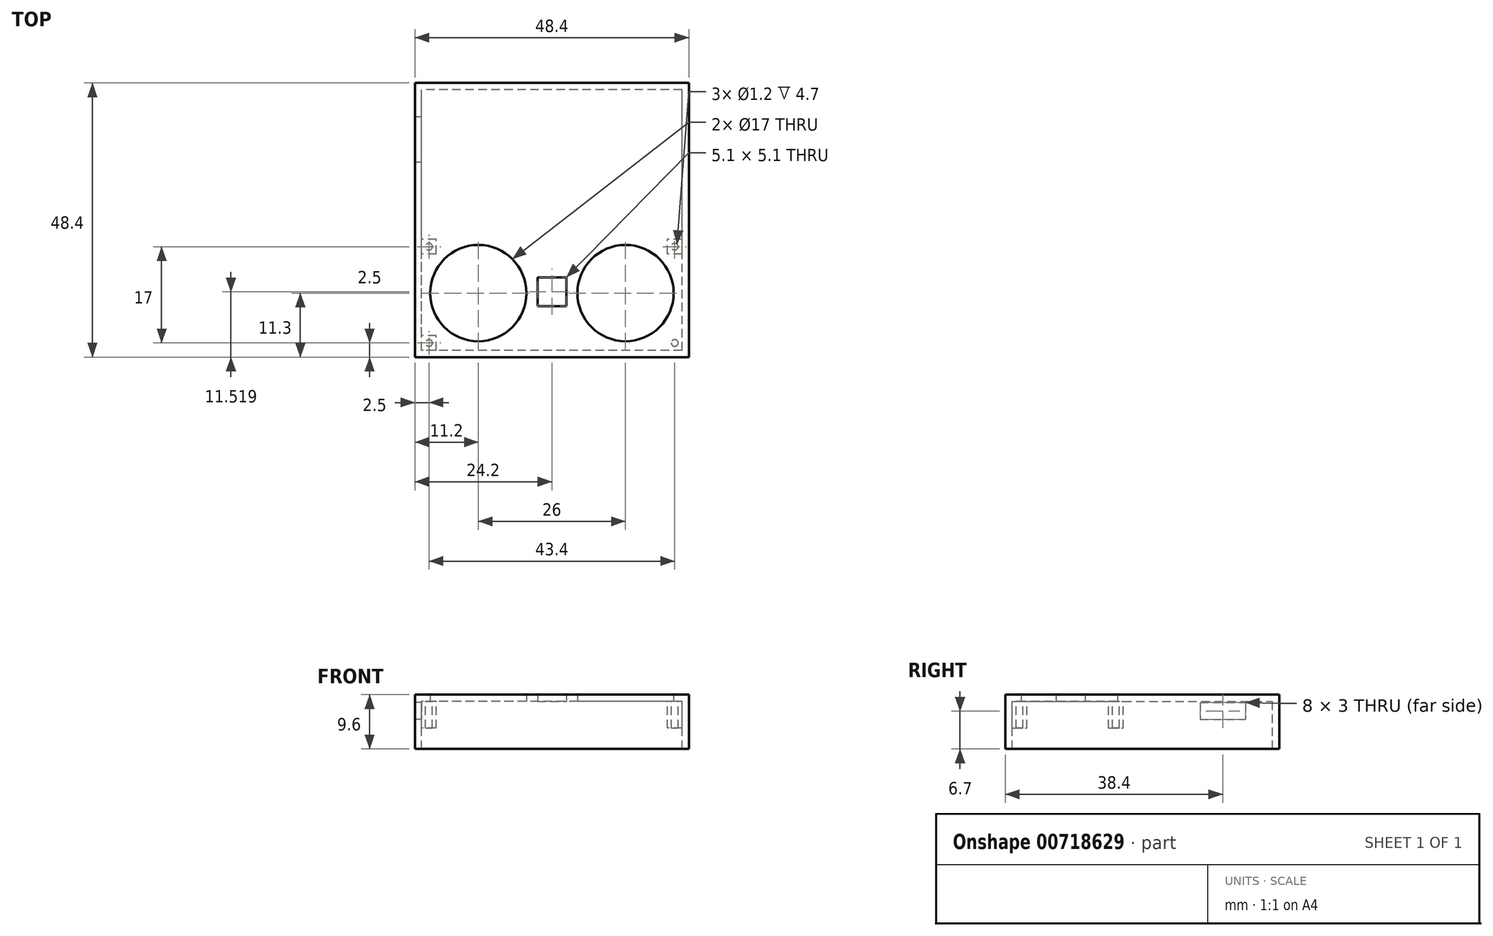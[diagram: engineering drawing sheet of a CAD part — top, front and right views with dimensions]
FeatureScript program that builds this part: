
annotation { "Feature Type Name" : "Feature", "Feature Type Description" : "" }
export const myFeature = defineFeature(function(context is Context, id is Id, definition is map)
    precondition{}
    {
        {
            var Q0;
            Q0=qCreatedBy(makeId("Top.planeOp"),FACE);
            var sketch = newSketch(context, id + "F0", { "sketchPlane" : qUnion([Q0])});
            skLineSegment(sketch, "E0.bottom", {"start": v(0, 0) * mm, "end": v(-23, 0) * mm});
            skLineSegment(sketch, "E0.top", {"start": v(0, 23) * mm, "end": v(-23, 23) * mm});
            skLineSegment(sketch, "E0.left", {"start": v(0, 0) * mm, "end": v(0, 23) * mm});
            skLineSegment(sketch, "E0.right", {"start": v(-23, 0) * mm, "end": v(-23, 23) * mm});
            skLineSegment(sketch, "E1.MirrorCS", {"start": v(-23, 0) * mm, "end": v(-23, -23) * mm});
            skLineSegment(sketch, "E2.MirrorCS", {"start": v(0, 0) * mm, "end": v(0, -23) * mm});
            skLineSegment(sketch, "E3.MirrorCS", {"start": v(0, -23) * mm, "end": v(-23, -23) * mm});
            skLineSegment(sketch, "E4.MirrorCS", {"start": v(0, 23) * mm, "end": v(23, 23) * mm});
            skLineSegment(sketch, "E5.MirrorCS", {"start": v(0, -23) * mm, "end": v(23, -23) * mm});
            skLineSegment(sketch, "E6.MirrorCS", {"start": v(23, 0) * mm, "end": v(23, 23) * mm});
            skLineSegment(sketch, "E7.MirrorCS", {"start": v(0, 0) * mm, "end": v(23, 0) * mm});
            skLineSegment(sketch, "E8.MirrorCS", {"start": v(23, 0) * mm, "end": v(23, -23) * mm});
            skCircle(sketch, "E9", {"center": v(13, -12.9) * mm, "radius": 8.5 * mm});
            skCircle(sketch, "E10", {"center": v(-13, -12.9) * mm, "radius": 8.5 * mm});
            skLineSegment(sketch, "E11.bottom", {"start": v(-2.55, -15.23) * mm, "end": v(2.55, -15.23) * mm});
            skLineSegment(sketch, "E11.top", {"start": v(-2.55, -10.13) * mm, "end": v(2.55, -10.13) * mm});
            skLineSegment(sketch, "E11.left", {"start": v(-2.55, -15.23) * mm, "end": v(-2.55, -10.13) * mm});
            skLineSegment(sketch, "E11.right", {"start": v(2.55, -15.23) * mm, "end": v(2.55, -10.13) * mm});
            skSolve(sketch);
        }
        {
            var Q0;
            {var subQ1=sQuery(id+"F0.wireOp",EDGE,"E0.top");Q0=makeQuery(id+"F0.imprint","IMPRINT",FACE,{"disambiguationData":[TD([[makeQuery(id+"F0.imprint","IMPRINT",EDGE,{"derivedFrom":subQ1}),1.0]])]});}
            var Q1;
            {var subQ1=sQuery(id+"F0.wireOp",EDGE,"E1.MirrorCS");Q1=makeQuery(id+"F0.imprint","IMPRINT",FACE,{"disambiguationData":[TD([[makeQuery(id+"F0.imprint","IMPRINT",EDGE,{"derivedFrom":subQ1}),1.0]])]});}
            var Q2;
            {var subQ7=sQuery(id+"F0.wireOp",EDGE,"E4.MirrorCS");Q2=makeQuery(id+"F0.imprint","IMPRINT",FACE,{"disambiguationData":[TD([[makeQuery(id+"F0.imprint","IMPRINT",EDGE,{"derivedFrom":subQ7}),-1.0]])]});}
            var Q3;
            {var subQ9=sQuery(id+"F0.wireOp",EDGE,"E5.MirrorCS");Q3=makeQuery(id+"F0.imprint","IMPRINT",FACE,{"disambiguationData":[TD([[makeQuery(id+"F0.imprint","IMPRINT",EDGE,{"derivedFrom":subQ9}),1.0]])]});}
            extrude(context, id + "F1", {"entities" : qUnion([Q0, Q1, Q2, Q3]), "endBound" : BoundingType.SYMMETRIC, "depth" : 1.2 * mm, "offsetDistance" : 25 * mm});
        }
        {
            var Q0;
            Q0=makeQuery(id+"F1.opExtrude","CAP_FACE",FACE,{"disambiguationData":[OSD([sQuery(id+"F0.wireOp",EDGE,"E0.top"),sQuery(id+"F0.wireOp",EDGE,"E0.right"),sQuery(id+"F0.wireOp",EDGE,"E1.MirrorCS"),sQuery(id+"F0.wireOp",EDGE,"E3.MirrorCS"),sQuery(id+"F0.wireOp",EDGE,"18OHl2Td-8SmV-nLja-3BuC-y3GKfxBrHoTz"),sQuery(id+"F0.wireOp",EDGE,"E4.MirrorCS"),sQuery(id+"F0.wireOp",EDGE,"f96b6ea1-77e4-4928-808a-502d4fa3524e1.MirrorC"),sQuery(id+"F0.wireOp",EDGE,"E5.MirrorCS"),sQuery(id+"F0.wireOp",EDGE,"E6.MirrorCS"),sQuery(id+"F0.wireOp",EDGE,"E8.MirrorCS"),sQuery(id+"F0.wireOp",EDGE,"ZzQ9hNgQ-oA48-EWd8-CxiW-ZcLfL0NBcqYF")])],"isStart":false});
            var sketch = newSketch(context, id + "F2", { "sketchPlane" : qUnion([Q0])});
            skLineSegment(sketch, "E12.0", {"start": v(23, 23) * mm, "end": v(-23, 23) * mm});
            skLineSegment(sketch, "E12.1", {"start": v(-23, -23) * mm, "end": v(-23, 23) * mm});
            skLineSegment(sketch, "E12.2", {"start": v(23, -23) * mm, "end": v(-23, -23) * mm});
            skLineSegment(sketch, "E12.3", {"start": v(23, -23) * mm, "end": v(23, 23) * mm});
            skPoint(sketch, "E12.4", {"position": v(0, 0) * mm});
            skLineSegment(sketch, "E13.bottom", {"start": v(0, 24.2) * mm, "end": v(-24.2, 24.2) * mm});
            skLineSegment(sketch, "E13.top", {"start": v(0, -24.2) * mm, "end": v(-24.2, -24.2) * mm});
            skLineSegment(sketch, "E13.left", {"start": v(0, 24.2) * mm, "end": v(0, -24.2) * mm});
            skLineSegment(sketch, "E13.right", {"start": v(-24.2, 24.2) * mm, "end": v(-24.2, -24.2) * mm});
            skLineSegment(sketch, "E14.MirrorCS", {"start": v(0, 24.2) * mm, "end": v(24.2, 24.2) * mm});
            skLineSegment(sketch, "E15.MirrorCS", {"start": v(24.2, 24.2) * mm, "end": v(24.2, -24.2) * mm});
            skLineSegment(sketch, "E16.MirrorCS", {"start": v(0, -24.2) * mm, "end": v(24.2, -24.2) * mm});
            skSolve(sketch);
        }
        {
            var Q0;
            {var subQ1=sQuery(id+"F2.wireOp",EDGE,"E12.1");Q0=makeQuery(id+"F2.imprint","IMPRINT",FACE,{"disambiguationData":[TD([[makeQuery(id+"F2.imprint","IMPRINT",EDGE,{"derivedFrom":subQ1}),1.0]])]});}
            var Q1;
            {var subQ4=sQuery(id+"F2.wireOp",EDGE,"E12.3");Q1=makeQuery(id+"F2.imprint","IMPRINT",FACE,{"disambiguationData":[TD([[makeQuery(id+"F2.imprint","IMPRINT",EDGE,{"derivedFrom":subQ4}),-1.0]])]});}
            extrude(context, id + "F3", {"entities" : qUnion([Q0, Q1]), "operationType" : NewBodyOperationType.ADD, "oppositeDirection" : true, "depth" : 9.6 * mm, "offsetDistance" : 25 * mm});
        }
        {
            var Q0;
            Q0=makeQuery(id+"F1.opExtrude","CAP_FACE",FACE,{"disambiguationData":[OSD([sQuery(id+"F0.wireOp",EDGE,"E0.top"),sQuery(id+"F0.wireOp",EDGE,"E0.right"),sQuery(id+"F0.wireOp",EDGE,"E1.MirrorCS"),sQuery(id+"F0.wireOp",EDGE,"E3.MirrorCS"),sQuery(id+"F0.wireOp",EDGE,"18OHl2Td-8SmV-nLja-3BuC-y3GKfxBrHoTz"),sQuery(id+"F0.wireOp",EDGE,"E4.MirrorCS"),sQuery(id+"F0.wireOp",EDGE,"f96b6ea1-77e4-4928-808a-502d4fa3524e1.MirrorC"),sQuery(id+"F0.wireOp",EDGE,"E5.MirrorCS"),sQuery(id+"F0.wireOp",EDGE,"E6.MirrorCS"),sQuery(id+"F0.wireOp",EDGE,"E8.MirrorCS"),sQuery(id+"F0.wireOp",EDGE,"ZzQ9hNgQ-oA48-EWd8-CxiW-ZcLfL0NBcqYF")])],"isStart":true});
            var sketch = newSketch(context, id + "F4", { "sketchPlane" : qUnion([Q0])});
            skLineSegment(sketch, "E17.0", {"start": v(23, 23) * mm, "end": v(-23, 23) * mm});
            skLineSegment(sketch, "E17.1", {"start": v(-23, 23) * mm, "end": v(-23, -23) * mm});
            skLineSegment(sketch, "E17.2", {"start": v(23, -23) * mm, "end": v(-23, -23) * mm});
            skLineSegment(sketch, "E17.3", {"start": v(23, 23) * mm, "end": v(23, -23) * mm});
            skLineSegment(sketch, "E18", {"start": v(-21.7, 23) * mm, "end": v(-21.7, 21.7) * mm, "construction": true});
            skLineSegment(sketch, "E19", {"start": v(-21.7, 21.7) * mm, "end": v(-23, 21.7) * mm, "construction": true});
            skCircle(sketch, "E20", {"center": v(-21.7, 21.7) * mm, "radius": 0.6 * mm});
            skCircle(sketch, "E21.MirrorC", {"center": v(21.7, 21.7) * mm, "radius": 0.6 * mm});
            skLineSegment(sketch, "E22.bottom", {"start": v(-20.4, 23) * mm, "end": v(-23, 23) * mm});
            skLineSegment(sketch, "E22.top", {"start": v(-20.4, 20.4) * mm, "end": v(-23, 20.4) * mm});
            skLineSegment(sketch, "E22.left", {"start": v(-20.4, 23) * mm, "end": v(-20.4, 20.4) * mm});
            skLineSegment(sketch, "E22.right", {"start": v(-23, 23) * mm, "end": v(-23, 20.4) * mm});
            skLineSegment(sketch, "E23.MirrorCS", {"start": v(20.4, 23) * mm, "end": v(20.4, 20.4) * mm});
            skLineSegment(sketch, "E24.MirrorCS", {"start": v(20.4, 20.4) * mm, "end": v(23, 20.4) * mm});
            skLineSegment(sketch, "E25", {"start": v(-21.7, 6) * mm, "end": v(-21.7, 4.7) * mm, "construction": true});
            skLineSegment(sketch, "E26", {"start": v(-21.7, 4.7) * mm, "end": v(-23, 4.7) * mm, "construction": true});
            skCircle(sketch, "E27", {"center": v(-21.7, 4.7) * mm, "radius": 0.6 * mm});
            skLineSegment(sketch, "E28.bottom", {"start": v(-20.4, 6) * mm, "end": v(-23, 6) * mm});
            skLineSegment(sketch, "E28.top", {"start": v(-20.4, 3.4) * mm, "end": v(-23, 3.4) * mm});
            skLineSegment(sketch, "E28.left", {"start": v(-20.4, 6) * mm, "end": v(-20.4, 3.4) * mm});
            skLineSegment(sketch, "E28.right", {"start": v(-23, 6) * mm, "end": v(-23, 3.4) * mm});
            skLineSegment(sketch, "E29", {"start": v(21.7, 6) * mm, "end": v(21.7, 4.7) * mm, "construction": true});
            skLineSegment(sketch, "E30", {"start": v(21.7, 4.7) * mm, "end": v(20.4, 4.7) * mm, "construction": true});
            skCircle(sketch, "E31", {"center": v(21.7, 4.7) * mm, "radius": 0.6 * mm});
            skLineSegment(sketch, "E32.bottom", {"start": v(23, 6) * mm, "end": v(20.4, 6) * mm});
            skLineSegment(sketch, "E32.top", {"start": v(23, 3.4) * mm, "end": v(20.4, 3.4) * mm});
            skLineSegment(sketch, "E32.left", {"start": v(23, 6) * mm, "end": v(23, 3.4) * mm});
            skLineSegment(sketch, "E32.right", {"start": v(20.4, 6) * mm, "end": v(20.4, 3.4) * mm});
            skSolve(sketch);
        }
        {
            var Q0;
            Q0=makeQuery(id+"F4.imprint","IMPRINT",FACE,{"disambiguationData":[TD([[makeQuery(id+"F4.imprint","IMPRINT",EDGE,{"derivedFrom":sQuery(id+"F4.wireOp",EDGE,"E21.MirrorC")}),1.0]])]});
            var Q1;
            Q1=makeQuery(id+"F4.imprint","IMPRINT",FACE,{"disambiguationData":[TD([[makeQuery(id+"F4.imprint","IMPRINT",EDGE,{"derivedFrom":sQuery(id+"F4.wireOp",EDGE,"E20")}),-1.0]])]});
            var Q2;
            Q2=makeQuery(id+"F4.imprint","IMPRINT",FACE,{"disambiguationData":[TD([[makeQuery(id+"F4.imprint","IMPRINT",EDGE,{"derivedFrom":sQuery(id+"F4.wireOp",EDGE,"E27")}),-1.0]])]});
            var Q3;
            Q3=makeQuery(id+"F4.imprint","IMPRINT",FACE,{"disambiguationData":[TD([[makeQuery(id+"F4.imprint","IMPRINT",EDGE,{"derivedFrom":sQuery(id+"F4.wireOp",EDGE,"E31")}),-1.0]])]});
            extrude(context, id + "F5", {"entities" : qUnion([Q0, Q1, Q2, Q3]), "operationType" : NewBodyOperationType.ADD, "depth" : 4.7 * mm, "offsetDistance" : 25 * mm});
        }
        {
            var Q0;
            Q0=makeQuery(id+"F3.opExtrude","SWEPT_FACE",FACE,{"disambiguationData":[OSD([sQuery(id+"F2.wireOp",EDGE,"E13.right")])]});
            var sketch = newSketch(context, id + "F6", { "sketchPlane" : qUnion([Q0])});
            skLineSegment(sketch, "E33.bottom", {"start": v(-18.2, -3.8) * mm, "end": v(-10.2, -3.8) * mm});
            skLineSegment(sketch, "E33.top", {"start": v(-18.2, -0.8) * mm, "end": v(-10.2, -0.8) * mm});
            skLineSegment(sketch, "E33.left", {"start": v(-18.2, -3.8) * mm, "end": v(-18.2, -0.8) * mm});
            skLineSegment(sketch, "E33.right", {"start": v(-10.2, -3.8) * mm, "end": v(-10.2, -0.8) * mm});
            skSolve(sketch);
        }
        {
            var Q0;
            Q0 = qSketchRegion(id + "F6", true);
            extrude(context, id + "F7", {"entities" : qUnion([Q0]), "operationType" : NewBodyOperationType.REMOVE, "oppositeDirection" : true, "depth" : 1.4 * mm, "offsetDistance" : 25 * mm});
        }
    });
